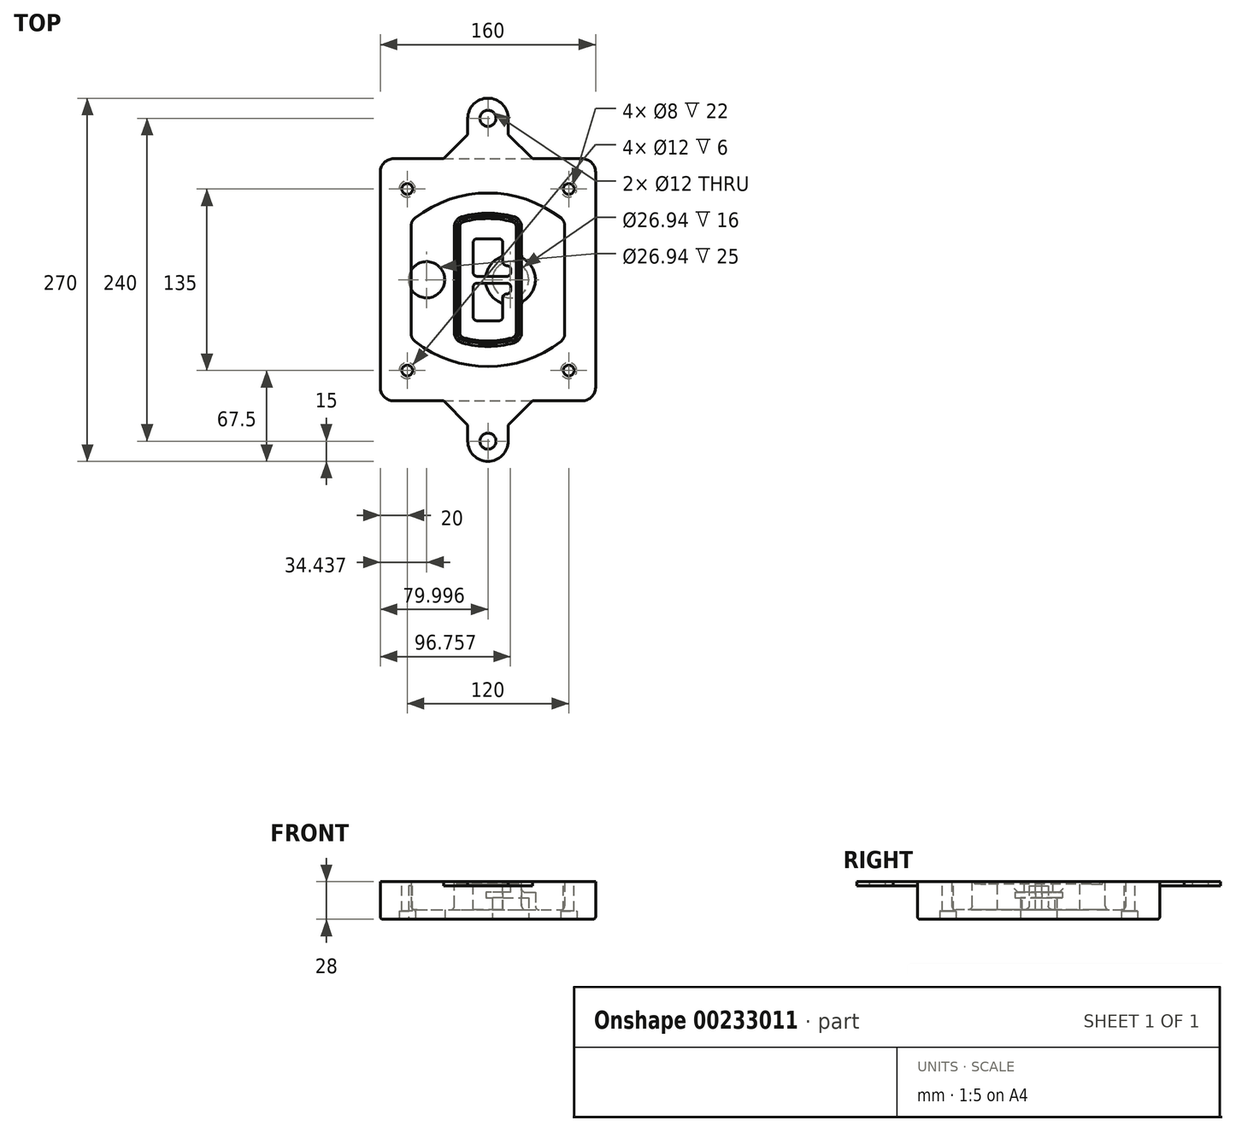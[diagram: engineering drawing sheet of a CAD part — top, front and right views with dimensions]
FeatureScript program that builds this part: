
annotation { "Feature Type Name" : "Feature", "Feature Type Description" : "" }
export const myFeature = defineFeature(function(context is Context, id is Id, definition is map)
    precondition{}
    {
        {
            var Q0;
            Q0=qCreatedBy(makeId("Top.planeOp"),FACE);
            var sketch = newSketch(context, id + "F0", { "sketchPlane" : qUnion([Q0])});
            skPoint(sketch, "E0.rect.middle", {"position": v(0, 0) * mm});
            skLineSegment(sketch, "E1.bottom", {"start": v(-70, -90) * mm, "end": v(70, -90) * mm});
            skLineSegment(sketch, "E1.top", {"start": v(-70, 90) * mm, "end": v(70, 90) * mm});
            skLineSegment(sketch, "E1.left", {"start": v(-80, -80) * mm, "end": v(-80, 80) * mm});
            skLineSegment(sketch, "E1.right", {"start": v(80, -80) * mm, "end": v(80, 80) * mm});
            skLineSegment(sketch, "E2", {"start": v(-80, 90) * mm, "end": v(80, -90) * mm, "construction": true});
            skLineSegment(sketch, "E3", {"start": v(80, 90) * mm, "end": v(-80, -90) * mm, "construction": true});
            skCircle(sketch, "E4", {"center": v(-60, 67.5) * mm, "radius": 4 * mm});
            skCircle(sketch, "E5", {"center": v(60, 67.5) * mm, "radius": 4 * mm});
            skCircle(sketch, "E6", {"center": v(60, -67.5) * mm, "radius": 4 * mm});
            skCircle(sketch, "E7", {"center": v(-60, -67.5) * mm, "radius": 4 * mm});
            skLineSegment(sketch, "E8", {"start": v(-60, 67.5) * mm, "end": v(60, 67.5) * mm, "construction": true});
            skLineSegment(sketch, "E9", {"start": v(60, 67.5) * mm, "end": v(60, -67.5) * mm, "construction": true});
            skLineSegment(sketch, "E10", {"start": v(60, -67.5) * mm, "end": v(-60, -67.5) * mm, "construction": true});
            skLineSegment(sketch, "E11", {"start": v(-60, -67.5) * mm, "end": v(-60, 67.5) * mm, "construction": true});
            skLineSegment(sketch, "E12", {"start": v(-60, 40.3) * mm, "end": v(-60, -40.3) * mm});
            skLineSegment(sketch, "E13", {"start": v(60, 40.3) * mm, "end": v(60, -40.3) * mm});
            skArc(sketch, "E14", {"start": v(56.15, 48.18) * mm, "mid": v(0, 67.5) * mm, "end": v(-56.15, 48.18) * mm});
            skArc(sketch, "E15", {"start": v(-56.15, -48.18) * mm, "mid": v(0, -67.5) * mm, "end": v(56.15, -48.18) * mm});
            skLineSegment(sketch, "E16", {"start": v(-60, 0) * mm, "end": v(60, 0) * mm, "construction": true});
            skPoint(sketch, "E17.visualSharp", {"position": v(-60, -45) * mm});
            skArc(sketch, "E17.filletArc", {"start": v(-60, -40.3) * mm, "mid": v(-58.99, -44.68) * mm, "end": v(-56.15, -48.18) * mm});
            skPoint(sketch, "E18.visualSharp", {"position": v(-60, 45) * mm});
            skArc(sketch, "E18.filletArc", {"start": v(-56.15, 48.18) * mm, "mid": v(-58.99, 44.68) * mm, "end": v(-60, 40.3) * mm});
            skPoint(sketch, "E19.visualSharp", {"position": v(60, 45) * mm});
            skArc(sketch, "E19.filletArc", {"start": v(60, 40.3) * mm, "mid": v(58.99, 44.68) * mm, "end": v(56.15, 48.18) * mm});
            skPoint(sketch, "E20.visualSharp", {"position": v(60, -45) * mm});
            skArc(sketch, "E20.filletArc", {"start": v(56.15, -48.18) * mm, "mid": v(58.99, -44.68) * mm, "end": v(60, -40.3) * mm});
            skPoint(sketch, "E21.visualSharp", {"position": v(-80, 90) * mm});
            skArc(sketch, "E21.filletArc", {"start": v(-70, 90) * mm, "mid": v(-77.07, 87.07) * mm, "end": v(-80, 80) * mm});
            skPoint(sketch, "E22.visualSharp", {"position": v(80, 90) * mm});
            skArc(sketch, "E22.filletArc", {"start": v(80, 80) * mm, "mid": v(77.07, 87.07) * mm, "end": v(70, 90) * mm});
            skPoint(sketch, "E23.visualSharp", {"position": v(80, -90) * mm});
            skArc(sketch, "E23.filletArc", {"start": v(70, -90) * mm, "mid": v(77.07, -87.07) * mm, "end": v(80, -80) * mm});
            skPoint(sketch, "E24.visualSharp", {"position": v(-80, -90) * mm});
            skArc(sketch, "E24.filletArc", {"start": v(-80, -80) * mm, "mid": v(-77.07, -87.07) * mm, "end": v(-70, -90) * mm});
            skArc(sketch, "E25.0", {"start": v(57, 40.3) * mm, "mid": v(56.3, 43.36) * mm, "end": v(54.3, 45.81) * mm});
            skLineSegment(sketch, "E25.1", {"start": v(57, 40.3) * mm, "end": v(57, -40.3) * mm});
            skArc(sketch, "E25.2", {"start": v(54.3, -45.81) * mm, "mid": v(56.3, -43.36) * mm, "end": v(57, -40.3) * mm});
            skArc(sketch, "E25.3", {"start": v(-54.3, -45.81) * mm, "mid": v(0, -64.5) * mm, "end": v(54.3, -45.81) * mm});
            skArc(sketch, "E25.4", {"start": v(-57, -40.3) * mm, "mid": v(-56.3, -43.36) * mm, "end": v(-54.3, -45.81) * mm});
            skArc(sketch, "E25.5", {"start": v(54.3, 45.81) * mm, "mid": v(0, 64.5) * mm, "end": v(-54.3, 45.81) * mm});
            skLineSegment(sketch, "E25.6", {"start": v(-57, 40.3) * mm, "end": v(-57, -40.3) * mm});
            skArc(sketch, "E25.7", {"start": v(-54.3, 45.81) * mm, "mid": v(-56.3, 43.36) * mm, "end": v(-57, 40.3) * mm});
            skArc(sketch, "E26.0", {"start": v(-58.62, 51.33) * mm, "mid": v(-62.58, 46.43) * mm, "end": v(-64, 40.3) * mm});
            skArc(sketch, "E26.1", {"start": v(58.62, 51.33) * mm, "mid": v(0, 71.5) * mm, "end": v(-58.62, 51.33) * mm});
            skArc(sketch, "E26.2", {"start": v(64, 40.3) * mm, "mid": v(62.58, 46.43) * mm, "end": v(58.62, 51.33) * mm});
            skLineSegment(sketch, "E26.3", {"start": v(64, 40.3) * mm, "end": v(64, -40.3) * mm});
            skArc(sketch, "E26.4", {"start": v(58.62, -51.33) * mm, "mid": v(62.58, -46.43) * mm, "end": v(64, -40.3) * mm});
            skLineSegment(sketch, "E26.5", {"start": v(-64, 40.3) * mm, "end": v(-64, -40.3) * mm});
            skArc(sketch, "E26.6", {"start": v(-58.62, -51.33) * mm, "mid": v(0, -71.5) * mm, "end": v(58.62, -51.33) * mm});
            skArc(sketch, "E26.7", {"start": v(-64, -40.3) * mm, "mid": v(-62.58, -46.43) * mm, "end": v(-58.62, -51.33) * mm});
            skSolve(sketch);
        }
        {
            var Q0;
            Q0=makeQuery(id+"F0.imprint","IMPRINT",FACE,{"disambiguationData":[TD([[makeQuery(id+"F0.imprint","IMPRINT",EDGE,{"derivedFrom":sQuery(id+"F0.wireOp",EDGE,"E1.bottom")}),1.0]])]});
            var Q1;
            Q1=makeQuery(id+"F0.imprint","IMPRINT",FACE,{"disambiguationData":[TD([[makeQuery(id+"F0.imprint","IMPRINT",EDGE,{"derivedFrom":sQuery(id+"F0.wireOp",EDGE,"E12")}),1.0]])]});
            var Q2;
            Q2=makeQuery(id+"F0.imprint","IMPRINT",FACE,{"disambiguationData":[TD([[makeQuery(id+"F0.imprint","IMPRINT",EDGE,{"derivedFrom":sQuery(id+"F0.wireOp",EDGE,"E25.0")}),1.0]])]});
            var Q3;
            Q3=makeQuery(id+"F0.imprint","IMPRINT",FACE,{"disambiguationData":[TD([[makeQuery(id+"F0.imprint","IMPRINT",EDGE,{"derivedFrom":sQuery(id+"F0.wireOp",EDGE,"E12")}),-1.0]])]});
            extrude(context, id + "F1", {"entities" : qUnion([Q0, Q1, Q2, Q3]), "oppositeDirection" : true, "depth" : 25 * mm});
        }
        {
            var Q0;
            Q0=makeQuery(id+"F0.imprint","IMPRINT",FACE,{"disambiguationData":[TD([[makeQuery(id+"F0.imprint","IMPRINT",EDGE,{"derivedFrom":sQuery(id+"F0.wireOp",EDGE,"E12")}),1.0]])]});
            extrude(context, id + "F2", {"entities" : qUnion([Q0]), "operationType" : NewBodyOperationType.ADD, "depth" : 3 * mm});
        }
        {
            var Q0;
            Q0=makeQuery(id+"F0.imprint","IMPRINT",FACE,{"disambiguationData":[TD([[makeQuery(id+"F0.imprint","IMPRINT",EDGE,{"derivedFrom":sQuery(id+"F0.wireOp",EDGE,"E25.0")}),1.0]])]});
            extrude(context, id + "F3", {"entities" : qUnion([Q0]), "operationType" : NewBodyOperationType.REMOVE, "oppositeDirection" : true, "depth" : 18 * mm});
        }
        {
            var Q0;
            Q0=makeQuery(id+"F2.opExtrude","CAP_FACE",FACE,{"disambiguationData":[OSD([sQuery(id+"F0.wireOp",EDGE,"E12"),sQuery(id+"F0.wireOp",EDGE,"E13"),sQuery(id+"F0.wireOp",EDGE,"E14"),sQuery(id+"F0.wireOp",EDGE,"E15"),sQuery(id+"F0.wireOp",EDGE,"E17.filletArc"),sQuery(id+"F0.wireOp",EDGE,"E18.filletArc"),sQuery(id+"F0.wireOp",EDGE,"E19.filletArc"),sQuery(id+"F0.wireOp",EDGE,"E20.filletArc"),sQuery(id+"F0.wireOp",EDGE,"E25.0"),sQuery(id+"F0.wireOp",EDGE,"E25.1"),sQuery(id+"F0.wireOp",EDGE,"E25.2"),sQuery(id+"F0.wireOp",EDGE,"E25.3"),sQuery(id+"F0.wireOp",EDGE,"E25.4"),sQuery(id+"F0.wireOp",EDGE,"E25.5"),sQuery(id+"F0.wireOp",EDGE,"E25.6"),sQuery(id+"F0.wireOp",EDGE,"E25.7")])],"isStart":false});
            var sketch = newSketch(context, id + "F4", { "sketchPlane" : qUnion([Q0])});
            skArc(sketch, "E27.0", {"start": v(-19.08, -46.97) * mm, "mid": v(0, -49.5) * mm, "end": v(19.08, -46.97) * mm});
            skArc(sketch, "E28.0", {"start": v(19.08, 46.97) * mm, "mid": v(0, 49.5) * mm, "end": v(-19.08, 46.97) * mm});
            skLineSegment(sketch, "E29", {"start": v(-25, 39.25) * mm, "end": v(-25, -39.25) * mm});
            skLineSegment(sketch, "E30", {"start": v(25, 39.25) * mm, "end": v(25, -39.25) * mm});
            skLineSegment(sketch, "E31", {"start": v(-25, 45.1) * mm, "end": v(25, 45.1) * mm, "construction": true});
            skLineSegment(sketch, "E32", {"start": v(-25, -45.1) * mm, "end": v(25, -45.1) * mm, "construction": true});
            skPoint(sketch, "E33.visualSharp", {"position": v(-25, 45.1) * mm});
            skArc(sketch, "E33.filletArc", {"start": v(-19.08, 46.97) * mm, "mid": v(-23.35, 44.11) * mm, "end": v(-25, 39.25) * mm});
            skPoint(sketch, "E34.visualSharp", {"position": v(25, 45.1) * mm});
            skArc(sketch, "E34.filletArc", {"start": v(25, 39.25) * mm, "mid": v(23.35, 44.11) * mm, "end": v(19.08, 46.97) * mm});
            skPoint(sketch, "E35.visualSharp", {"position": v(25, -45.1) * mm});
            skArc(sketch, "E35.filletArc", {"start": v(19.08, -46.97) * mm, "mid": v(23.35, -44.11) * mm, "end": v(25, -39.25) * mm});
            skPoint(sketch, "E36.visualSharp", {"position": v(-25, -45.1) * mm});
            skArc(sketch, "E36.filletArc", {"start": v(-25, -39.25) * mm, "mid": v(-23.35, -44.11) * mm, "end": v(-19.08, -46.97) * mm});
            skArc(sketch, "E37.0", {"start": v(54.3, 45.81) * mm, "mid": v(0, 64.5) * mm, "end": v(-54.3, 45.81) * mm});
            skArc(sketch, "E37.1", {"start": v(-54.3, 45.81) * mm, "mid": v(-56.3, 43.36) * mm, "end": v(-57, 40.3) * mm});
            skLineSegment(sketch, "E37.2", {"start": v(-57, 40.3) * mm, "end": v(-57, -40.3) * mm});
            skArc(sketch, "E37.3", {"start": v(-57, -40.3) * mm, "mid": v(-56.3, -43.36) * mm, "end": v(-54.3, -45.81) * mm});
            skArc(sketch, "E37.4", {"start": v(-54.3, -45.81) * mm, "mid": v(0, -64.5) * mm, "end": v(54.3, -45.81) * mm});
            skArc(sketch, "E37.5", {"start": v(54.3, -45.81) * mm, "mid": v(56.3, -43.36) * mm, "end": v(57, -40.3) * mm});
            skLineSegment(sketch, "E37.6", {"start": v(57, 40.3) * mm, "end": v(57, -40.3) * mm});
            skArc(sketch, "E37.7", {"start": v(57, 40.3) * mm, "mid": v(56.3, 43.36) * mm, "end": v(54.3, 45.81) * mm});
            skLineSegment(sketch, "E38.0", {"start": v(23, 39.25) * mm, "end": v(23, -39.25) * mm});
            skArc(sketch, "E38.1", {"start": v(18.56, -45.04) * mm, "mid": v(21.76, -42.9) * mm, "end": v(23, -39.25) * mm});
            skArc(sketch, "E38.2", {"start": v(-18.56, -45.04) * mm, "mid": v(0, -47.5) * mm, "end": v(18.56, -45.04) * mm});
            skArc(sketch, "E38.3", {"start": v(-23, -39.25) * mm, "mid": v(-21.76, -42.9) * mm, "end": v(-18.56, -45.04) * mm});
            skLineSegment(sketch, "E38.4", {"start": v(-23, 39.25) * mm, "end": v(-23, -39.25) * mm});
            skArc(sketch, "E38.5", {"start": v(23, 39.25) * mm, "mid": v(21.76, 42.9) * mm, "end": v(18.56, 45.04) * mm});
            skArc(sketch, "E38.6", {"start": v(-18.56, 45.04) * mm, "mid": v(-21.76, 42.9) * mm, "end": v(-23, 39.25) * mm});
            skArc(sketch, "E38.7", {"start": v(18.56, 45.04) * mm, "mid": v(0, 47.5) * mm, "end": v(-18.56, 45.04) * mm});
            skArc(sketch, "E39.0", {"start": v(21, 39.25) * mm, "mid": v(20.18, 41.68) * mm, "end": v(18.04, 43.1) * mm});
            skLineSegment(sketch, "E39.1", {"start": v(21, 39.25) * mm, "end": v(21, -39.25) * mm});
            skArc(sketch, "E39.2", {"start": v(18.04, -43.1) * mm, "mid": v(20.18, -41.68) * mm, "end": v(21, -39.25) * mm});
            skArc(sketch, "E39.3", {"start": v(-18.04, -43.1) * mm, "mid": v(0, -45.5) * mm, "end": v(18.04, -43.1) * mm});
            skArc(sketch, "E39.4", {"start": v(-21, -39.25) * mm, "mid": v(-20.18, -41.68) * mm, "end": v(-18.04, -43.1) * mm});
            skArc(sketch, "E39.5", {"start": v(18.04, 43.1) * mm, "mid": v(0, 45.5) * mm, "end": v(-18.04, 43.1) * mm});
            skLineSegment(sketch, "E39.6", {"start": v(-21, 39.25) * mm, "end": v(-21, -39.25) * mm});
            skArc(sketch, "E39.7", {"start": v(-18.04, 43.1) * mm, "mid": v(-20.18, 41.68) * mm, "end": v(-21, 39.25) * mm});
            skLineSegment(sketch, "E40", {"start": v(-25, 0) * mm, "end": v(25, 0) * mm, "construction": true});
            skLineSegment(sketch, "E41", {"start": v(-11, 5.5) * mm, "end": v(-11, 27.5) * mm});
            skLineSegment(sketch, "E42", {"start": v(-8, 30.5) * mm, "end": v(8, 30.5) * mm});
            skLineSegment(sketch, "E43", {"start": v(11, 27.5) * mm, "end": v(11, 13.5) * mm});
            skLineSegment(sketch, "E44", {"start": v(14, 10.5) * mm, "end": v(14, 10.5) * mm});
            skLineSegment(sketch, "E45", {"start": v(17, 7.5) * mm, "end": v(17, 5.5) * mm});
            skLineSegment(sketch, "E46", {"start": v(14, 2.5) * mm, "end": v(-8, 2.5) * mm});
            skPoint(sketch, "E47.visualSharp", {"position": v(-11, 30.5) * mm});
            skArc(sketch, "E47.filletArc", {"start": v(-8, 30.5) * mm, "mid": v(-10.12, 29.62) * mm, "end": v(-11, 27.5) * mm});
            skPoint(sketch, "E48.visualSharp", {"position": v(11, 30.5) * mm});
            skArc(sketch, "E48.filletArc", {"start": v(11, 27.5) * mm, "mid": v(10.12, 29.62) * mm, "end": v(8, 30.5) * mm});
            skPoint(sketch, "E49.visualSharp", {"position": v(11, 10.5) * mm});
            skArc(sketch, "E49.filletArc", {"start": v(11, 13.5) * mm, "mid": v(11.88, 11.38) * mm, "end": v(14, 10.5) * mm});
            skPoint(sketch, "E50.visualSharp", {"position": v(17, 10.5) * mm});
            skArc(sketch, "E50.filletArc", {"start": v(17, 7.5) * mm, "mid": v(16.12, 9.62) * mm, "end": v(14, 10.5) * mm});
            skPoint(sketch, "E51.visualSharp", {"position": v(17, 2.5) * mm});
            skArc(sketch, "E51.filletArc", {"start": v(14, 2.5) * mm, "mid": v(16.12, 3.38) * mm, "end": v(17, 5.5) * mm});
            skPoint(sketch, "E52.visualSharp", {"position": v(-11, 2.5) * mm});
            skArc(sketch, "E52.filletArc", {"start": v(-11, 5.5) * mm, "mid": v(-10.12, 3.38) * mm, "end": v(-8, 2.5) * mm});
            skLineSegment(sketch, "E53.0.MirrorCS", {"start": v(14, -2.5) * mm, "end": v(-8, -2.5) * mm});
            skArc(sketch, "E54.0.MirrorCS", {"start": v(-11, -5.5) * mm, "mid": v(-10.12, -3.38) * mm, "end": v(-8, -2.5) * mm});
            skLineSegment(sketch, "E55.0.MirrorCS", {"start": v(-11, -5.5) * mm, "end": v(-11, -27.5) * mm});
            skArc(sketch, "E56.0.MirrorCS", {"start": v(-8, -30.5) * mm, "mid": v(-10.12, -29.62) * mm, "end": v(-11, -27.5) * mm});
            skLineSegment(sketch, "E57.0.MirrorCS", {"start": v(-8, -30.5) * mm, "end": v(8, -30.5) * mm});
            skArc(sketch, "E58.0.MirrorCS", {"start": v(11, -27.5) * mm, "mid": v(10.12, -29.62) * mm, "end": v(8, -30.5) * mm});
            skLineSegment(sketch, "E59.0.MirrorCS", {"start": v(11, -27.5) * mm, "end": v(11, -13.5) * mm});
            skArc(sketch, "E60.0.MirrorCS", {"start": v(11, -13.5) * mm, "mid": v(11.88, -11.38) * mm, "end": v(14, -10.5) * mm});
            skArc(sketch, "E61.0.MirrorCS", {"start": v(17, -7.5) * mm, "mid": v(16.12, -9.62) * mm, "end": v(14, -10.5) * mm});
            skLineSegment(sketch, "E62.0.MirrorCS", {"start": v(17, -7.5) * mm, "end": v(17, -5.5) * mm});
            skArc(sketch, "E63.0.MirrorCS", {"start": v(14, -2.5) * mm, "mid": v(16.12, -3.38) * mm, "end": v(17, -5.5) * mm});
            skSolve(sketch);
        }
        {
            var Q0;
            Q0=makeQuery(id+"F4.imprint","IMPRINT",FACE,{"disambiguationData":[TD([[makeQuery(id+"F4.imprint","IMPRINT",EDGE,{"derivedFrom":sQuery(id+"F4.wireOp",EDGE,"E27.0")}),1.0]])]});
            var Q1;
            Q1=makeQuery(id+"F4.imprint","IMPRINT",FACE,{"disambiguationData":[TD([[makeQuery(id+"F4.imprint","IMPRINT",EDGE,{"derivedFrom":sQuery(id+"F4.wireOp",EDGE,"E38.0")}),-1.0]])]});
            var Q2;
            Q2=makeQuery(id+"F4.imprint","IMPRINT",FACE,{"disambiguationData":[TD([[makeQuery(id+"F4.imprint","IMPRINT",EDGE,{"derivedFrom":sQuery(id+"F4.wireOp",EDGE,"E39.0")}),1.0]])]});
            extrude(context, id + "F5", {"entities" : qUnion([Q0, Q1, Q2]), "operationType" : NewBodyOperationType.ADD, "endBound" : BoundingType.UP_TO_NEXT, "oppositeDirection" : true, "depth" : 25 * mm});
        }
        {
            var Q0;
            Q0=makeQuery(id+"F4.imprint","IMPRINT",FACE,{"disambiguationData":[TD([[makeQuery(id+"F4.imprint","IMPRINT",EDGE,{"derivedFrom":sQuery(id+"F4.wireOp",EDGE,"E38.0")}),-1.0]])]});
            extrude(context, id + "F6", {"entities" : qUnion([Q0]), "operationType" : NewBodyOperationType.REMOVE, "oppositeDirection" : true, "depth" : 2 * mm});
        }
        {
            var Q0;
            Q0=makeQuery(id+"F1.opExtrude","CAP_FACE",FACE,{"disambiguationData":[OSD([sQuery(id+"F0.wireOp",EDGE,"E1.bottom"),sQuery(id+"F0.wireOp",EDGE,"E1.top"),sQuery(id+"F0.wireOp",EDGE,"E1.left"),sQuery(id+"F0.wireOp",EDGE,"E1.right"),sQuery(id+"F0.wireOp",EDGE,"E4"),sQuery(id+"F0.wireOp",EDGE,"E5"),sQuery(id+"F0.wireOp",EDGE,"E6"),sQuery(id+"F0.wireOp",EDGE,"E7"),sQuery(id+"F0.wireOp",EDGE,"E21.filletArc"),sQuery(id+"F0.wireOp",EDGE,"E22.filletArc"),sQuery(id+"F0.wireOp",EDGE,"E23.filletArc"),sQuery(id+"F0.wireOp",EDGE,"E24.filletArc")])],"isStart":false});
            var sketch = newSketch(context, id + "F7", { "sketchPlane" : qUnion([Q0])});
            skCircle(sketch, "E64", {"center": v(16.76, 0) * mm, "radius": 13.47 * mm});
            skCircle(sketch, "E65", {"center": v(-45.56, 0) * mm, "radius": 13.47 * mm});
            skLineSegment(sketch, "E66", {"start": v(80, 0) * mm, "end": v(-80, 0) * mm});
            skCircle(sketch, "E67", {"center": v(16.76, 0) * mm, "radius": 18.47 * mm});
            skCircle(sketch, "E68", {"center": v(60, -67.5) * mm, "radius": 6 * mm});
            skCircle(sketch, "E69", {"center": v(-60, -67.5) * mm, "radius": 6 * mm});
            skCircle(sketch, "E70", {"center": v(-60, 67.5) * mm, "radius": 6 * mm});
            skCircle(sketch, "E71", {"center": v(60, 67.5) * mm, "radius": 6 * mm});
            skSolve(sketch);
        }
        {
            var Q0;
            {var subQ1=sQuery(id+"F7.wireOp",EDGE,"E66");var subQ4=sQuery(id+"F7.wireOp",EDGE,"E64");var subQ6=makeQuery(id+"F7.imprint","INTERSECT",VERTEX,{"disambiguationData":[OD(0.0)],"derivedFrom":[subQ4,subQ1]});Q0=makeQuery(id+"F7.imprint","IMPRINT",FACE,{"disambiguationData":[TD([[makeQuery(id+"F7.imprint","IMPRINT",EDGE,{"disambiguationData":[TD([[subQ6,-1.0]])],"derivedFrom":subQ4}),-1.0]])]});}
            var Q1;
            {var subQ0=sQuery(id+"F7.wireOp",EDGE,"E66");var subQ1=sQuery(id+"F7.wireOp",EDGE,"E64");var subQ3=makeQuery(id+"F7.imprint","INTERSECT",VERTEX,{"disambiguationData":[OD(0.0)],"derivedFrom":[subQ1,subQ0]});Q1=makeQuery(id+"F7.imprint","IMPRINT",FACE,{"disambiguationData":[TD([[makeQuery(id+"F7.imprint","IMPRINT",EDGE,{"disambiguationData":[TD([[subQ3,-1.0]])],"derivedFrom":subQ1}),1.0]])]});}
            var Q2;
            {var subQ0=sQuery(id+"F7.wireOp",EDGE,"E66");var subQ1=sQuery(id+"F7.wireOp",EDGE,"E64");var subQ3=makeQuery(id+"F7.imprint","INTERSECT",VERTEX,{"disambiguationData":[OD(0.0)],"derivedFrom":[subQ1,subQ0]});Q2=makeQuery(id+"F7.imprint","IMPRINT",FACE,{"disambiguationData":[TD([[makeQuery(id+"F7.imprint","IMPRINT",EDGE,{"disambiguationData":[TD([[subQ3,1.0]])],"derivedFrom":subQ1}),1.0]])]});}
            var Q3;
            {var subQ1=sQuery(id+"F7.wireOp",EDGE,"E66");var subQ4=sQuery(id+"F7.wireOp",EDGE,"E64");var subQ6=makeQuery(id+"F7.imprint","INTERSECT",VERTEX,{"disambiguationData":[OD(0.0)],"derivedFrom":[subQ4,subQ1]});Q3=makeQuery(id+"F7.imprint","IMPRINT",FACE,{"disambiguationData":[TD([[makeQuery(id+"F7.imprint","IMPRINT",EDGE,{"disambiguationData":[TD([[subQ6,1.0]])],"derivedFrom":subQ4}),-1.0]])]});}
            extrude(context, id + "F8", {"entities" : qUnion([Q0, Q1, Q2, Q3]), "operationType" : NewBodyOperationType.ADD, "oppositeDirection" : true, "depth" : 20 * mm});
        }
        {
            var Q0;
            {var subQ0=sQuery(id+"F7.wireOp",EDGE,"E66");var subQ1=sQuery(id+"F7.wireOp",EDGE,"E64");var subQ3=makeQuery(id+"F7.imprint","INTERSECT",VERTEX,{"disambiguationData":[OD(0.0)],"derivedFrom":[subQ1,subQ0]});Q0=makeQuery(id+"F7.imprint","IMPRINT",FACE,{"disambiguationData":[TD([[makeQuery(id+"F7.imprint","IMPRINT",EDGE,{"disambiguationData":[TD([[subQ3,-1.0]])],"derivedFrom":subQ1}),1.0]])]});}
            var Q1;
            {var subQ0=sQuery(id+"F7.wireOp",EDGE,"E66");var subQ1=sQuery(id+"F7.wireOp",EDGE,"E64");var subQ3=makeQuery(id+"F7.imprint","INTERSECT",VERTEX,{"disambiguationData":[OD(0.0)],"derivedFrom":[subQ1,subQ0]});Q1=makeQuery(id+"F7.imprint","IMPRINT",FACE,{"disambiguationData":[TD([[makeQuery(id+"F7.imprint","IMPRINT",EDGE,{"disambiguationData":[TD([[subQ3,1.0]])],"derivedFrom":subQ1}),1.0]])]});}
            extrude(context, id + "F9", {"entities" : qUnion([Q0, Q1]), "operationType" : NewBodyOperationType.REMOVE, "oppositeDirection" : true, "depth" : 16 * mm});
        }
        {
            var Q0;
            {var subQ0=sQuery(id+"F7.wireOp",EDGE,"E66");var subQ1=sQuery(id+"F7.wireOp",EDGE,"E65");var subQ3=makeQuery(id+"F7.imprint","INTERSECT",VERTEX,{"disambiguationData":[OD(0.0)],"derivedFrom":[subQ1,subQ0]});Q0=makeQuery(id+"F7.imprint","IMPRINT",FACE,{"disambiguationData":[TD([[makeQuery(id+"F7.imprint","IMPRINT",EDGE,{"disambiguationData":[TD([[subQ3,-1.0]])],"derivedFrom":subQ1}),1.0]])]});}
            var Q1;
            {var subQ0=sQuery(id+"F7.wireOp",EDGE,"E66");var subQ1=sQuery(id+"F7.wireOp",EDGE,"E65");var subQ3=makeQuery(id+"F7.imprint","INTERSECT",VERTEX,{"disambiguationData":[OD(0.0)],"derivedFrom":[subQ1,subQ0]});Q1=makeQuery(id+"F7.imprint","IMPRINT",FACE,{"disambiguationData":[TD([[makeQuery(id+"F7.imprint","IMPRINT",EDGE,{"disambiguationData":[TD([[subQ3,1.0]])],"derivedFrom":subQ1}),1.0]])]});}
            extrude(context, id + "F10", {"entities" : qUnion([Q0, Q1]), "operationType" : NewBodyOperationType.REMOVE, "oppositeDirection" : true, "depth" : 25 * mm});
        }
        {
            var Q0;
            Q0=makeQuery(id+"F7.imprint","IMPRINT",FACE,{"disambiguationData":[TD([[makeQuery(id+"F7.imprint","IMPRINT",EDGE,{"derivedFrom":sQuery(id+"F7.wireOp",EDGE,"E68")}),1.0]])]});
            var Q1;
            Q1=makeQuery(id+"F7.imprint","IMPRINT",FACE,{"disambiguationData":[TD([[makeQuery(id+"F7.imprint","IMPRINT",EDGE,{"derivedFrom":makeQuery(id+"F1.opExtrude","CAP_EDGE",EDGE,{"disambiguationData":[OSD([sQuery(id+"F0.wireOp",EDGE,"E5")])],"isStart":false})}),-1.0]])]});
            var Q2;
            Q2=makeQuery(id+"F7.imprint","IMPRINT",FACE,{"disambiguationData":[TD([[makeQuery(id+"F7.imprint","IMPRINT",EDGE,{"derivedFrom":sQuery(id+"F7.wireOp",EDGE,"E69")}),1.0]])]});
            var Q3;
            Q3=makeQuery(id+"F7.imprint","IMPRINT",FACE,{"disambiguationData":[TD([[makeQuery(id+"F7.imprint","IMPRINT",EDGE,{"derivedFrom":makeQuery(id+"F1.opExtrude","CAP_EDGE",EDGE,{"disambiguationData":[OSD([sQuery(id+"F0.wireOp",EDGE,"E4")])],"isStart":false})}),-1.0]])]});
            var Q4;
            Q4=makeQuery(id+"F7.imprint","IMPRINT",FACE,{"disambiguationData":[TD([[makeQuery(id+"F7.imprint","IMPRINT",EDGE,{"derivedFrom":sQuery(id+"F7.wireOp",EDGE,"E70")}),1.0]])]});
            var Q5;
            Q5=makeQuery(id+"F7.imprint","IMPRINT",FACE,{"disambiguationData":[TD([[makeQuery(id+"F7.imprint","IMPRINT",EDGE,{"derivedFrom":makeQuery(id+"F1.opExtrude","CAP_EDGE",EDGE,{"disambiguationData":[OSD([sQuery(id+"F0.wireOp",EDGE,"E7")])],"isStart":false})}),-1.0]])]});
            var Q6;
            Q6=makeQuery(id+"F7.imprint","IMPRINT",FACE,{"disambiguationData":[TD([[makeQuery(id+"F7.imprint","IMPRINT",EDGE,{"derivedFrom":sQuery(id+"F7.wireOp",EDGE,"E71")}),1.0]])]});
            var Q7;
            Q7=makeQuery(id+"F7.imprint","IMPRINT",FACE,{"disambiguationData":[TD([[makeQuery(id+"F7.imprint","IMPRINT",EDGE,{"derivedFrom":makeQuery(id+"F1.opExtrude","CAP_EDGE",EDGE,{"disambiguationData":[OSD([sQuery(id+"F0.wireOp",EDGE,"E6")])],"isStart":false})}),-1.0]])]});
            extrude(context, id + "F11", {"entities" : qUnion([Q0, Q1, Q2, Q3, Q4, Q5, Q6, Q7]), "operationType" : NewBodyOperationType.REMOVE, "oppositeDirection" : true, "depth" : 6 * mm});
        }
        {
            var Q0;
            Q0=makeQuery(id+"F9.boolean.opBoolean","COPY",FACE,{"derivedFrom":makeQuery(id+"F9.opExtrude","CAP_FACE",FACE,{"disambiguationData":[OSD([sQuery(id+"F7.wireOp",EDGE,"E64")])],"isStart":false})});
            var sketch = newSketch(context, id + "F12", { "sketchPlane" : qUnion([Q0])});
            skArc(sketch, "E72.0", {"start": v(11, 17.55) * mm, "mid": v(2.57, 11.82) * mm, "end": v(-1.54, 2.5) * mm});
            skArc(sketch, "E72.1", {"start": v(-1.54, -2.5) * mm, "mid": v(2.57, -11.82) * mm, "end": v(11, -17.55) * mm});
            skLineSegment(sketch, "E73", {"start": v(-1.54, -2.5) * mm, "end": v(14, -2.5) * mm});
            skLineSegment(sketch, "E74.0", {"start": v(14, 2.5) * mm, "end": v(-1.54, 2.5) * mm});
            skArc(sketch, "E74.1", {"start": v(14, 2.5) * mm, "mid": v(16.12, 3.38) * mm, "end": v(17, 5.5) * mm});
            skLineSegment(sketch, "E74.2", {"start": v(17, 7.5) * mm, "end": v(17, 5.5) * mm});
            skArc(sketch, "E74.3", {"start": v(17, 7.5) * mm, "mid": v(16.12, 9.62) * mm, "end": v(14, 10.5) * mm});
            skArc(sketch, "E74.4", {"start": v(11, 13.5) * mm, "mid": v(11.88, 11.38) * mm, "end": v(14, 10.5) * mm});
            skLineSegment(sketch, "E74.5", {"start": v(11, 17.55) * mm, "end": v(11, 13.5) * mm});
            skLineSegment(sketch, "E74.7", {"start": v(14, -2.5) * mm, "end": v(-1.54, -2.5) * mm});
            skArc(sketch, "E74.8", {"start": v(14, -2.5) * mm, "mid": v(16.12, -3.38) * mm, "end": v(17, -5.5) * mm});
            skLineSegment(sketch, "E74.9", {"start": v(17, -7.5) * mm, "end": v(17, -5.5) * mm});
            skArc(sketch, "E74.10", {"start": v(17, -7.5) * mm, "mid": v(16.12, -9.62) * mm, "end": v(14, -10.5) * mm});
            skArc(sketch, "E74.11", {"start": v(11, -13.5) * mm, "mid": v(11.88, -11.38) * mm, "end": v(14, -10.5) * mm});
            skLineSegment(sketch, "E74.12", {"start": v(11, -17.55) * mm, "end": v(11, -13.5) * mm});
            skPoint(sketch, "E75.orphan", {"position": v(11, -27.5) * mm});
            skPoint(sketch, "E76.orphan", {"position": v(-8, -2.5) * mm});
            skPoint(sketch, "E77.orphan", {"position": v(-8, 2.5) * mm});
            skPoint(sketch, "E78.orphan", {"position": v(11, 27.5) * mm});
            skSolve(sketch);
        }
        {
            var Q0;
            {var subQ7=sQuery(id+"F12.wireOp",EDGE,"E72.0");var subQ14=sQuery(id+"F12.wireOp",EDGE,"E72.1");var subQ16=sQuery(id+"F12.wireOp",EDGE,"E74.1");var subQ18=sQuery(id+"F12.wireOp",EDGE,"E74.8");Q0=qUnion([makeQuery(id+"F12.imprint","IMPRINT",FACE,{"disambiguationData":[TD([[makeQuery(id+"F12.imprint","IMPRINT",EDGE,{"derivedFrom":subQ7}),1.0]])]}),makeQuery(id+"F12.imprint","IMPRINT",FACE,{"disambiguationData":[TD([[makeQuery(id+"F12.imprint","IMPRINT",EDGE,{"derivedFrom":subQ14}),1.0]])]}),makeQuery(id+"F12.imprint","IMPRINT",FACE,{"disambiguationData":[TD([[makeQuery(id+"F12.imprint","IMPRINT",EDGE,{"derivedFrom":subQ16}),1.0]])]}),makeQuery(id+"F12.imprint","IMPRINT",FACE,{"disambiguationData":[TD([[makeQuery(id+"F12.imprint","IMPRINT",EDGE,{"derivedFrom":subQ18}),-1.0]])]})]);}
            var Q1;
            Q1=makeQuery(id+"F5.boolean.opBoolean","SPLIT",FACE,{"disambiguationData":[TD([makeQuery(id+"F5.opExtrude","SWEPT_FACE",FACE,{"disambiguationData":[OSD([sQuery(id+"F4.wireOp",EDGE,"E41")])]})])],"derivedFrom":makeQuery(id+"F3.boolean.opBoolean","COPY",FACE,{"derivedFrom":makeQuery(id+"F3.opExtrude","CAP_FACE",FACE,{"disambiguationData":[OSD([sQuery(id+"F0.wireOp",EDGE,"E25.0"),sQuery(id+"F0.wireOp",EDGE,"E25.1"),sQuery(id+"F0.wireOp",EDGE,"E25.2"),sQuery(id+"F0.wireOp",EDGE,"E25.3"),sQuery(id+"F0.wireOp",EDGE,"E25.4"),sQuery(id+"F0.wireOp",EDGE,"E25.5"),sQuery(id+"F0.wireOp",EDGE,"E25.6"),sQuery(id+"F0.wireOp",EDGE,"E25.7")])],"isStart":false})})});
            extrude(context, id + "F13", {"entities" : qUnion([Q0]), "operationType" : NewBodyOperationType.REMOVE, "endBound" : BoundingType.UP_TO_SURFACE, "endBoundEntityFace" : qUnion([Q1]), "depth" : 25 * mm});
        }
        {
            var Q0;
            Q0=makeQuery(id+"F3.boolean.opBoolean","COPY",EDGE,{"derivedFrom":makeQuery(id+"F3.opExtrude","CAP_EDGE",EDGE,{"disambiguationData":[OSD([sQuery(id+"F0.wireOp",EDGE,"E25.6")])],"isStart":false})});
            var Q1;
            Q1=makeQuery(id+"F8.boolean.opBoolean","INTERSECT",EDGE,{"derivedFrom":[makeQuery(id+"F5.opExtrude","SWEPT_FACE",FACE,{"disambiguationData":[OSD([sQuery(id+"F4.wireOp",EDGE,"E30")])]}),makeQuery(id+"F8.opExtrude","CAP_FACE",FACE,{"disambiguationData":[OSD([sQuery(id+"F7.wireOp",EDGE,"E67")])],"isStart":false})]});
            var Q2;
            Q2=makeQuery(id+"F8.boolean.opBoolean","INTERSECT",EDGE,{"disambiguationData":[OD(1.0)],"derivedFrom":[makeQuery(id+"F5.opExtrude","SWEPT_FACE",FACE,{"disambiguationData":[OSD([sQuery(id+"F4.wireOp",EDGE,"E30")])]}),makeQuery(id+"F8.opExtrude","SWEPT_FACE",FACE,{"disambiguationData":[OSD([sQuery(id+"F7.wireOp",EDGE,"E67")])]})]});
            var Q3;
            {var subQ0=sQuery(id+"F4.wireOp",EDGE,"E30");Q3=makeQuery(id+"F8.boolean.opBoolean","SPLIT",EDGE,{"disambiguationData":[TD([makeQuery(id+"F5.opExtrude","SWEPT_FACE",FACE,{"disambiguationData":[OSD([sQuery(id+"F4.wireOp",EDGE,"E35.filletArc")])]})])],"derivedFrom":makeQuery(id+"F5.opExtrude","CAP_EDGE",EDGE,{"disambiguationData":[OSD([subQ0])],"isStart":false})});}
            var Q4;
            {var subQ0=sQuery(id+"F0.wireOp",EDGE,"E25.7");var subQ1=sQuery(id+"F0.wireOp",EDGE,"E25.1");var subQ2=sQuery(id+"F0.wireOp",EDGE,"E25.6");var subQ3=sQuery(id+"F0.wireOp",EDGE,"E25.5");var subQ4=sQuery(id+"F0.wireOp",EDGE,"E25.4");var subQ5=sQuery(id+"F0.wireOp",EDGE,"E25.0");var subQ6=sQuery(id+"F0.wireOp",EDGE,"E25.2");var subQ7=sQuery(id+"F0.wireOp",EDGE,"E25.3");Q4=makeQuery(id+"F8.boolean.opBoolean","INTERSECT",EDGE,{"derivedFrom":[makeQuery(id+"F5.boolean.opBoolean","SPLIT",FACE,{"disambiguationData":[TD([makeQuery(id+"F2.opExtrude","SWEPT_FACE",FACE,{"disambiguationData":[OSD([subQ5])]})])],"derivedFrom":makeQuery(id+"F3.boolean.opBoolean","COPY",FACE,{"derivedFrom":makeQuery(id+"F3.opExtrude","CAP_FACE",FACE,{"disambiguationData":[OSD([subQ5,subQ1,subQ6,subQ7,subQ4,subQ3,subQ2,subQ0])],"isStart":false})})}),makeQuery(id+"F8.opExtrude","SWEPT_FACE",FACE,{"disambiguationData":[OSD([sQuery(id+"F7.wireOp",EDGE,"E67")])]})]});}
            var Q5;
            Q5=makeQuery(id+"F8.boolean.opBoolean","INTERSECT",EDGE,{"disambiguationData":[OD(0.0)],"derivedFrom":[makeQuery(id+"F5.opExtrude","SWEPT_FACE",FACE,{"disambiguationData":[OSD([sQuery(id+"F4.wireOp",EDGE,"E30")])]}),makeQuery(id+"F8.opExtrude","SWEPT_FACE",FACE,{"disambiguationData":[OSD([sQuery(id+"F7.wireOp",EDGE,"E67")])]})]});
            fillet(context, id + "F14", {"entities" : qUnion([Q0, Q1, Q2, Q3, Q4, Q5]), "radius" : 3 * mm, "tangentPropagation" : true, "allowEdgeOverflow" : false});
        }
        {
            var Q0;
            Q0=makeQuery(id+"F1.opExtrude","CAP_EDGE",EDGE,{"disambiguationData":[OSD([sQuery(id+"F0.wireOp",EDGE,"E1.bottom")])],"isStart":false});
            fillet(context, id + "F15", {"entities" : qUnion([Q0]), "radius" : 2 * mm, "tangentPropagation" : true, "allowEdgeOverflow" : false});
        }
        {
            var Q0;
            {var subQ0=sQuery(id+"F0.wireOp",EDGE,"E22.filletArc");var subQ1=sQuery(id+"F0.wireOp",EDGE,"E7");var subQ2=sQuery(id+"F0.wireOp",EDGE,"E6");var subQ3=sQuery(id+"F0.wireOp",EDGE,"E5");var subQ4=sQuery(id+"F0.wireOp",EDGE,"E4");var subQ5=sQuery(id+"F0.wireOp",EDGE,"E1.bottom");var subQ6=sQuery(id+"F0.wireOp",EDGE,"E21.filletArc");var subQ7=sQuery(id+"F0.wireOp",EDGE,"E1.top");var subQ8=sQuery(id+"F0.wireOp",EDGE,"E1.left");var subQ9=sQuery(id+"F0.wireOp",EDGE,"E1.right");var subQ10=sQuery(id+"F0.wireOp",EDGE,"E23.filletArc");var subQ11=sQuery(id+"F0.wireOp",EDGE,"E24.filletArc");Q0=makeQuery(id+"F2.boolean.opBoolean","SPLIT",FACE,{"disambiguationData":[TD([makeQuery(id+"F1.opExtrude","SWEPT_FACE",FACE,{"disambiguationData":[OSD([subQ5])]})])],"derivedFrom":makeQuery(id+"F1.opExtrude","CAP_FACE",FACE,{"disambiguationData":[OSD([subQ5,subQ7,subQ8,subQ9,subQ4,subQ3,subQ2,subQ1,subQ6,subQ0,subQ10,subQ11])],"isStart":true})});}
            var sketch = newSketch(context, id + "F16", { "sketchPlane" : qUnion([Q0])});
            skCircle(sketch, "E79", {"center": v(0, 120) * mm, "radius": 6 * mm});
            skArc(sketch, "E80", {"start": v(15, 120) * mm, "mid": v(0, 135) * mm, "end": v(-15, 120) * mm});
            skLineSegment(sketch, "E81", {"start": v(15, 120) * mm, "end": v(15, 108) * mm});
            skLineSegment(sketch, "E82", {"start": v(-15, 120) * mm, "end": v(-15, 108) * mm});
            skLineSegment(sketch, "E83", {"start": v(15, 108) * mm, "end": v(33, 90) * mm});
            skLineSegment(sketch, "E84", {"start": v(-15, 108) * mm, "end": v(-33, 90) * mm});
            skLineSegment(sketch, "E85", {"start": v(0, 120) * mm, "end": v(0, 90) * mm, "construction": true});
            skLineSegment(sketch, "E86", {"start": v(-80, 0) * mm, "end": v(80, 0) * mm, "construction": true});
            skLineSegment(sketch, "E87.MirrorCS", {"start": v(-15, -108) * mm, "end": v(-33, -90) * mm});
            skLineSegment(sketch, "E88.MirrorCS", {"start": v(15, -108) * mm, "end": v(33, -90) * mm});
            skLineSegment(sketch, "E89.MirrorCS", {"start": v(0, -120) * mm, "end": v(0, -90) * mm, "construction": true});
            skLineSegment(sketch, "E90.MirrorCS", {"start": v(-15, -120) * mm, "end": v(-15, -108) * mm});
            skLineSegment(sketch, "E91.MirrorCS", {"start": v(15, -120) * mm, "end": v(15, -108) * mm});
            skArc(sketch, "E92.MirrorCS", {"start": v(15, -120) * mm, "mid": v(0, -135) * mm, "end": v(-15, -120) * mm});
            skCircle(sketch, "E93.MirrorC", {"center": v(0, -120) * mm, "radius": 6 * mm});
            skSolve(sketch);
        }
        {
            var Q0;
            Q0=makeQuery(id+"F16.imprint","IMPRINT",FACE,{"disambiguationData":[TD([[makeQuery(id+"F16.imprint","IMPRINT",EDGE,{"derivedFrom":makeQuery(id+"F1.opExtrude","CAP_EDGE",EDGE,{"disambiguationData":[OSD([sQuery(id+"F0.wireOp",EDGE,"E1.left")])],"isStart":true})}),-1.0]])]});
            var Q1;
            Q1=makeQuery(id+"F16.imprint","IMPRINT",FACE,{"disambiguationData":[TD([[makeQuery(id+"F16.imprint","IMPRINT",EDGE,{"derivedFrom":sQuery(id+"F16.wireOp",EDGE,"E79")}),-1.0]])]});
            var Q2;
            {var subQ0=sQuery(id+"F16.wireOp",EDGE,"E87.MirrorCS");Q2=makeQuery(id+"F16.imprint","IMPRINT",FACE,{"disambiguationData":[TD([[makeQuery(id+"F16.imprint","IMPRINT",EDGE,{"derivedFrom":subQ0}),-1.0]])]});}
            var Q3;
            Q3=makeQuery(id+"F2.opExtrude","CAP_FACE",FACE,{"disambiguationData":[OSD([sQuery(id+"F0.wireOp",EDGE,"E12"),sQuery(id+"F0.wireOp",EDGE,"E13"),sQuery(id+"F0.wireOp",EDGE,"E14"),sQuery(id+"F0.wireOp",EDGE,"E15"),sQuery(id+"F0.wireOp",EDGE,"E17.filletArc"),sQuery(id+"F0.wireOp",EDGE,"E18.filletArc"),sQuery(id+"F0.wireOp",EDGE,"E19.filletArc"),sQuery(id+"F0.wireOp",EDGE,"E20.filletArc"),sQuery(id+"F0.wireOp",EDGE,"E25.0"),sQuery(id+"F0.wireOp",EDGE,"E25.1"),sQuery(id+"F0.wireOp",EDGE,"E25.2"),sQuery(id+"F0.wireOp",EDGE,"E25.3"),sQuery(id+"F0.wireOp",EDGE,"E25.4"),sQuery(id+"F0.wireOp",EDGE,"E25.5"),sQuery(id+"F0.wireOp",EDGE,"E25.6"),sQuery(id+"F0.wireOp",EDGE,"E25.7")])],"isStart":false});
            extrude(context, id + "F17", {"entities" : qUnion([Q0, Q1, Q2]), "operationType" : NewBodyOperationType.ADD, "endBound" : BoundingType.UP_TO_SURFACE, "endBoundEntityFace" : qUnion([Q3]), "depth" : 25 * mm});
        }
    });
